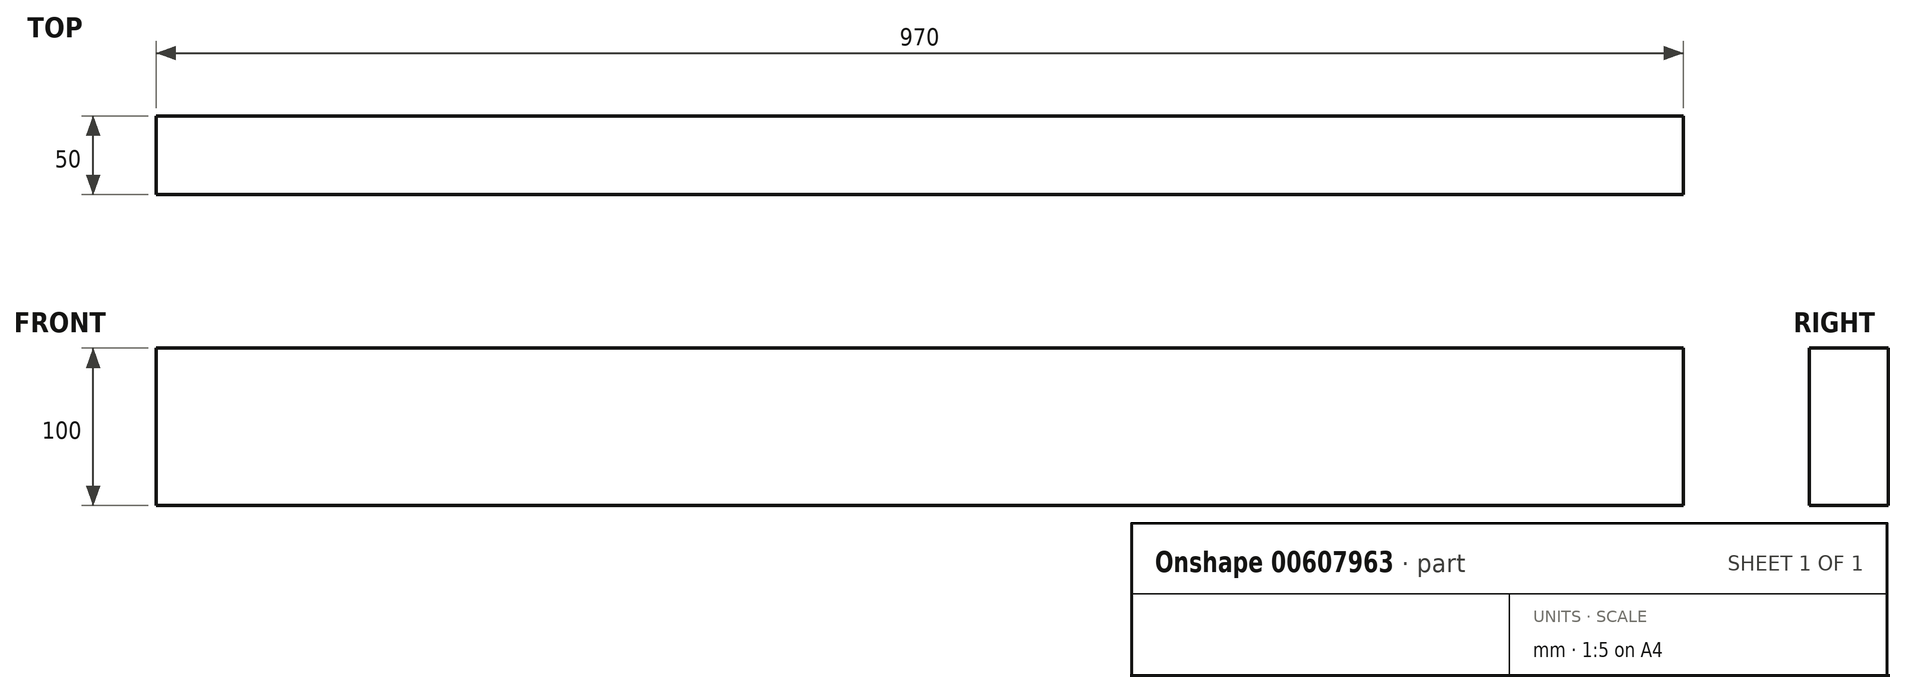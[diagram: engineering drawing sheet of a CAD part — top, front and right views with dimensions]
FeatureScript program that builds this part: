
annotation { "Feature Type Name" : "Feature", "Feature Type Description" : "" }
export const myFeature = defineFeature(function(context is Context, id is Id, definition is map)
    precondition{}
    {
        {
            var Q0;
            Q0=qCreatedBy(makeId("Front.planeOp"),FACE);
            var sketch = newSketch(context, id + "F0", { "sketchPlane" : qUnion([Q0])});
            skLineSegment(sketch, "E0.bottom", {"start": v(-485.4, 71.89) * mm, "end": v(484.6, 71.89) * mm});
            skLineSegment(sketch, "E0.top", {"start": v(-485.4, -28.11) * mm, "end": v(484.6, -28.11) * mm});
            skLineSegment(sketch, "E0.left", {"start": v(-485.4, 71.89) * mm, "end": v(-485.4, -28.11) * mm});
            skLineSegment(sketch, "E0.right", {"start": v(484.6, 71.89) * mm, "end": v(484.6, -28.11) * mm});
            skSolve(sketch);
        }
        {
            var Q0;
            Q0 = qSketchRegion(id + "F0", true);
            extrude(context, id + "F1", {"entities" : qUnion([Q0]), "depth" : 50 * mm, "offsetDistance" : 25 * mm});
        }
    });
